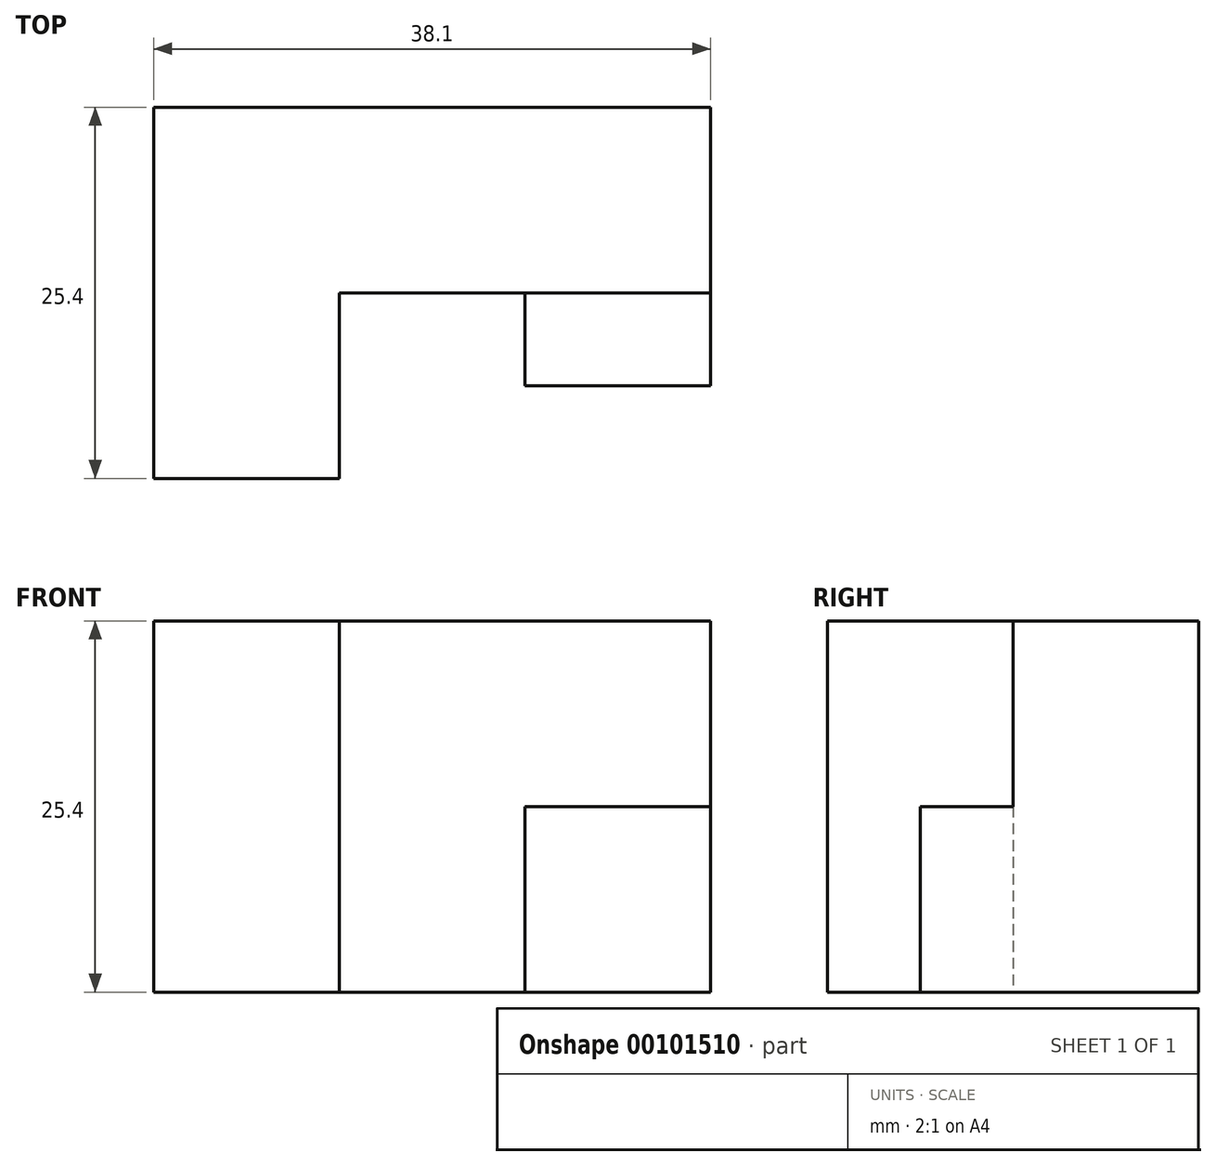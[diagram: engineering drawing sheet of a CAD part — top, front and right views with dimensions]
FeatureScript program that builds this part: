
annotation { "Feature Type Name" : "Feature", "Feature Type Description" : "" }
export const myFeature = defineFeature(function(context is Context, id is Id, definition is map)
    precondition{}
    {
        {
            var Q0;
            Q0=qCreatedBy(makeId("Top.planeOp"),FACE);
            var sketch = newSketch(context, id + "F0", { "sketchPlane" : qUnion([Q0])});
            skLineSegment(sketch, "E0", {"start": v(0, 0) * mm, "end": v(0, 25.4) * mm});
            skLineSegment(sketch, "E1", {"start": v(0, 25.4) * mm, "end": v(38.1, 25.4) * mm});
            skLineSegment(sketch, "E2", {"start": v(38.1, 25.4) * mm, "end": v(38.1, 12.7) * mm});
            skLineSegment(sketch, "E3", {"start": v(38.1, 12.7) * mm, "end": v(12.7, 12.7) * mm});
            skLineSegment(sketch, "E4", {"start": v(12.7, 12.7) * mm, "end": v(12.7, 0) * mm});
            skLineSegment(sketch, "E5", {"start": v(12.7, 0) * mm, "end": v(0, 0) * mm});
            skSolve(sketch);
        }
        {
            var Q0;
            Q0 = qSketchRegion(id + "F0", true);
            extrude(context, id + "F1", {"entities" : qUnion([Q0]), "depth" : 25.4 * mm});
        }
        {
            var Q0;
            Q0=qCreatedBy(makeId("Top.planeOp"),FACE);
            var sketch = newSketch(context, id + "F2", { "sketchPlane" : qUnion([Q0])});
            skLineSegment(sketch, "E6.bottom", {"start": v(38.1, 12.7) * mm, "end": v(25.4, 12.7) * mm});
            skLineSegment(sketch, "E6.top", {"start": v(38.1, 6.35) * mm, "end": v(25.4, 6.35) * mm});
            skLineSegment(sketch, "E6.left", {"start": v(38.1, 12.7) * mm, "end": v(38.1, 6.35) * mm});
            skLineSegment(sketch, "E6.right", {"start": v(25.4, 12.7) * mm, "end": v(25.4, 6.35) * mm});
            skSolve(sketch);
        }
        {
            var Q0;
            Q0 = qSketchRegion(id + "F2", true);
            extrude(context, id + "F3", {"entities" : qUnion([Q0]), "operationType" : NewBodyOperationType.ADD, "depth" : 12.7 * mm});
        }
    });
